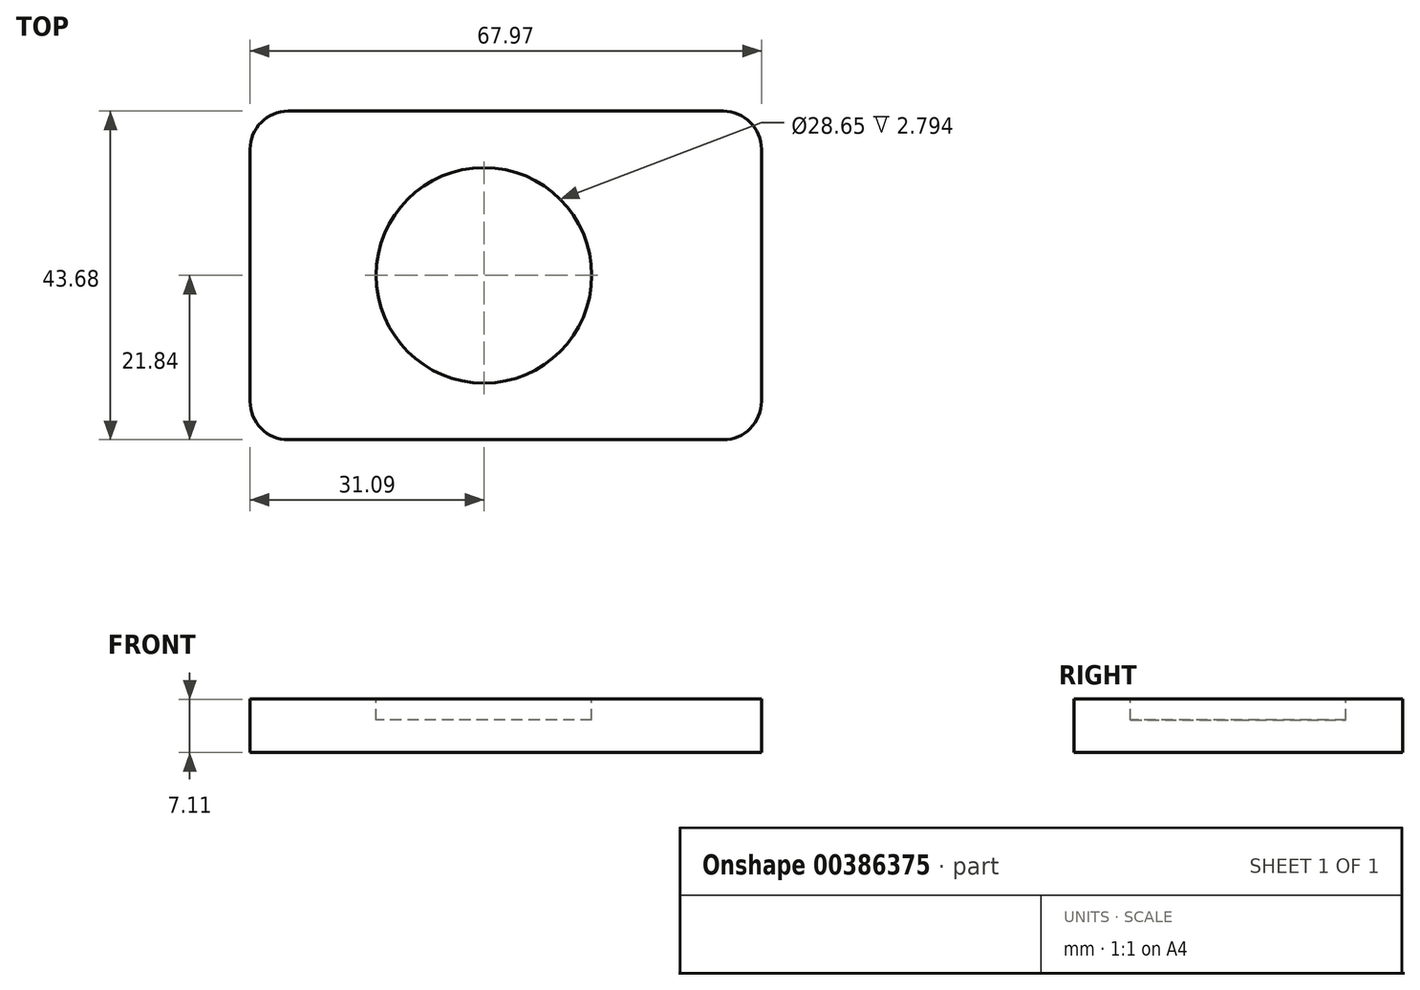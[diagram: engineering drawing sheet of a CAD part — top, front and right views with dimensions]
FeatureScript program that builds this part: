
annotation { "Feature Type Name" : "Feature", "Feature Type Description" : "" }
export const myFeature = defineFeature(function(context is Context, id is Id, definition is map)
    precondition{}
    {
        {
            var Q0;
            Q0=qCreatedBy(makeId("Top.planeOp"),FACE);
            var sketch = newSketch(context, id + "F0", { "sketchPlane" : qUnion([Q0])});
            skLineSegment(sketch, "E0.bottom", {"start": v(-31.1, 20.28) * mm, "end": v(36.88, 20.28) * mm});
            skLineSegment(sketch, "E0.top", {"start": v(-31.1, -23.4) * mm, "end": v(36.88, -23.4) * mm});
            skLineSegment(sketch, "E0.left", {"start": v(-31.1, 20.28) * mm, "end": v(-31.1, -23.4) * mm});
            skLineSegment(sketch, "E0.right", {"start": v(36.88, 20.28) * mm, "end": v(36.88, -23.4) * mm});
            skSolve(sketch);
        }
        {
            var Q0;
            Q0=makeQuery(id+"F0.imprint","IMPRINT",FACE,{"disambiguationData":[TD([[makeQuery(id+"F0.imprint","IMPRINT",EDGE,{"derivedFrom":sQuery(id+"F0.wireOp",EDGE,"E0.bottom")}),-1.0]])]});
            extrude(context, id + "F1", {"entities" : qUnion([Q0]), "depth" : 7.11 * mm});
        }
        {
            var Q0;
            Q0=makeQuery(id+"F1.opExtrude","SWEPT_EDGE",EDGE,{"disambiguationData":[OSD([sQuery(id+"F0.wireOp",EDGE,"E0.top"),sQuery(id+"F0.wireOp",EDGE,"E0.left")])]});
            var Q1;
            Q1=makeQuery(id+"F1.opExtrude","SWEPT_EDGE",EDGE,{"disambiguationData":[OSD([sQuery(id+"F0.wireOp",EDGE,"E0.top"),sQuery(id+"F0.wireOp",EDGE,"E0.right")])]});
            var Q2;
            Q2=makeQuery(id+"F1.opExtrude","SWEPT_EDGE",EDGE,{"disambiguationData":[OSD([sQuery(id+"F0.wireOp",EDGE,"E0.bottom"),sQuery(id+"F0.wireOp",EDGE,"E0.right")])]});
            var Q3;
            Q3=makeQuery(id+"F1.opExtrude","SWEPT_EDGE",EDGE,{"disambiguationData":[OSD([sQuery(id+"F0.wireOp",EDGE,"E0.bottom"),sQuery(id+"F0.wireOp",EDGE,"E0.left")])]});
            fillet(context, id + "F2", {"entities" : qUnion([Q0, Q1, Q2, Q3]), "radius" : 5.08 * mm, "tangentPropagation" : true, "allowEdgeOverflow" : false});
        }
        {
            var Q0;
            Q0=makeQuery(id+"F1.opExtrude","CAP_FACE",FACE,{"disambiguationData":[OSD([sQuery(id+"F0.wireOp",EDGE,"E0.bottom"),sQuery(id+"F0.wireOp",EDGE,"E0.top"),sQuery(id+"F0.wireOp",EDGE,"E0.left"),sQuery(id+"F0.wireOp",EDGE,"E0.right")])],"isStart":false});
            var sketch = newSketch(context, id + "F3", { "sketchPlane" : qUnion([Q0])});
            skCircle(sketch, "E1", {"center": v(0, -1.56) * mm, "radius": 14.33 * mm});
            skLineSegment(sketch, "E2", {"start": v(0, 20.28) * mm, "end": v(0, -23.4) * mm, "construction": true});
            skLineSegment(sketch, "E3", {"start": v(-31.1, -1.56) * mm, "end": v(36.88, -1.56) * mm, "construction": true});
            skSolve(sketch);
        }
        {
            var Q0;
            Q0=makeQuery(id+"F3.imprint","IMPRINT",FACE,{"disambiguationData":[TD([[makeQuery(id+"F3.imprint","IMPRINT",EDGE,{"derivedFrom":sQuery(id+"F3.wireOp",EDGE,"E1")}),1.0]])]});
            extrude(context, id + "F4", {"entities" : qUnion([Q0]), "operationType" : NewBodyOperationType.REMOVE, "oppositeDirection" : true, "depth" : 2.8 * mm});
        }
    });
